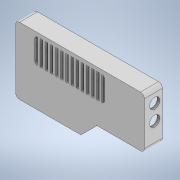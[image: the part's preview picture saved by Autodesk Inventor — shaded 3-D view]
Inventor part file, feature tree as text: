
AUTODESK INVENTOR PART (.ipt)
format: ipt  version: 2021 (Build 250183000, 183)  size: 543,744 bytes
history: native  units: mm
features: sketch x24, extrude x23, chamfer x5, fillet x3, hole x1
ambient origin geometry x8: Origin, YZ Plane, XZ Plane, XY Plane, X Axis, Y Axis, Z Axis, Center Point
bodies: Solid1 (feature_tree)
feature tree (56):
  extrude  "Extrusion1"  Depth=100.0mm
  extrude  "Extrusion3"  Depth=50.0mm
  extrude  "Extrusion4"  Depth=12.5mm
  extrude  "Extrusion12"  Depth=3.0mm TaperAngle=0.0deg
  extrude  "Extrusion13"  Depth=3.0mm TaperAngle=0.0deg
  fillet  "Fillet3"  Radius=2.0mm
  extrude  "Extrusion14"  Depth=2.0mm
  extrude  "Extrusion15"  Depth=44.0mm
  extrude  "Extrusion16"  Depth=12.0mm TaperAngle=0.0deg
  extrude  "Extrusion18"  Depth=12.6mm
  extrude  "Extrusion19"  Depth=3.0mm
  extrude  "Extrusion20"  Depth=1.5mm TaperAngle=0.0deg
  extrude  "Extrusion21"  Depth=4.4mm TaperAngle=0.0deg
  extrude  "Extrusion22"  Depth=2.0mm TaperAngle=0.0deg
  extrude  "Extrusion23"  Depth=14.0mm
  extrude  "Extrusion25"  Depth=4.4mm TaperAngle=0.0deg
  extrude  "Extrusion26"  Depth=4.0mm
  hole  "Hole2"  [1 undecoded]
  chamfer  "Chamfer3"  Distance=12.0mm
  chamfer  "Chamfer4"  Distance=12.0mm
  chamfer  "Chamfer5"  Distance=2.0mm
  chamfer  "Chamfer6"  Distance=12.0mm
  chamfer  "Chamfer7"  Distance=8.0mm
  extrude  "Extrusion27"  Depth=8.0mm
  fillet  "Fillet4"  Radius=8.0mm
  extrude  "Extrusion28"  Depth=2.0mm TaperAngle=0.0deg
  extrude  "Extrusion29"  Depth=1.6mm
  extrude  "Extrusion30"  Depth=0.5mm
  fillet  "Fillet5"  Radius=9.4mm
  extrude  "Extrusion31"  Depth=3.0mm
  extrude  "Extrusion32"  Depth=3.0mm
  extrude  "Extrusion33"  Depth=3.0mm
  sketch  "Sketch1"  dims[d0=52.0mm d1=100.0mm]
  sketch  "Sketch4"  dims[d2=26.0mm d3=50.0mm]
  sketch  "Sketch5"  dims[d4=2.0mm d5=0.0mm d35=12.5mm]
  sketch  "Sketch13"  dims[d36=63.1mm d37=3.0mm d38=0.0mm]
  sketch  "Sketch14"  dims[d39=50.673mm d40=3.0mm d41=0.0mm d79=2.0mm]
  sketch  "Sketch15"  dims[d80=2.0mm d81=2.0mm]
  sketch  "Sketch16"  dims[d82=1.2mm d83=44.0mm]
  sketch  "Sketch17"  dims[d84=59.0mm d85=12.0mm d86=0.0mm]
  sketch  "Sketch19"  dims[d87=2.0mm d88=12.6mm]
  sketch  "Sketch20"  dims[d89=12.0mm d90=0.0mm d91=3.0mm]
  sketch  "Sketch21"  dims[d92=7.8mm d93=1.5mm d94=0.0mm]
  sketch  "Sketch22"  dims[d95=33.8mm d96=4.4mm d97=0.0mm]
  sketch  "Sketch23"  dims[d98=2.0mm d99=2.0mm d100=0.0mm]
  sketch  "Sketch24"  dims[d108=3.0mm d109=14.0mm]
  sketch  "Sketch26"  dims[d110=10.0mm d111=4.4mm d112=0.0mm]
  sketch  "Sketch27"  dims[d113=1.3mm d114=4.0mm]
  sketch  "Sketch28"  dims[d115=3.0mm d116=0.0mm d117=2.0mm]
  sketch  "Sketch29"  dims[d118=2.0mm d119=12.0mm d120=0.0mm d121=12.0mm d122=0.0mm]
  sketch  "Sketch30"  dims[d123=70.0mm]
  sketch  "Sketch31"  dims[d124=89.0mm]
  sketch  "Sketch32"  dims[d125=8.0mm]
  sketch  "Sketch33"  dims[d126=8.0mm d127=2.0mm d128=0.0mm]
  sketch  "Sketch34"  dims[d129=8.0mm]
  sketch  "Sketch35"  dims[d130=10.0mm d131=12.0mm d132=8.0mm d133=8.0mm d134=8.0mm d135=2.0mm d136=0.0mm d140=1.6mm d141=0.5mm d142=9.4mm d143=0.0mm d144=3.0mm d145=3.0mm d146=3.0mm d147=50.0mm d148=97.0mm d149=15.0mm d150=3.0mm d151=3.0mm d152=97.0mm d153=49.0mm d154=4.8mm d155=4.8mm d156=4.8mm d157=4.8mm d158=4.8mm d159=5.0mm d160=0.0mm d161=2.0mm d162=6.0mm d163=4.0mm d164=2.0mm d165=90.0deg d166=4.0mm d167=20.594885mm d168=2.0mm d169=2.0mm d170=45.0deg d171=1.0mm d172=2.0mm d173=45.0deg d174=2.0mm d175=2.0mm d176=45.0deg d177=2.0mm d178=2.0mm d179=45.0deg d180=0.8mm d181=2.0mm d182=45.0deg d184=68.0mm d189=2.0mm d190=0.0mm d191=2.0mm d192=2.0mm d193=24.0mm d194=2.0mm d195=0.0mm d196=36.5mm d197=46.5mm d198=3.5mm d199=2.0mm d200=0.0mm d201=12.5mm d202=23.0mm d203=3.5mm d204=2.0mm d205=0.0mm d206=1.0mm d207=8.0mm d208=1.0mm d209=0.0mm d210=1.2mm d211=1.2mm d212=9.1mm d213=0.0mm d214=0.2mm d215=3.0mm d216=0.0mm d67=0.5mm d68=0.872665mm d69=0.5mm d70=0.872665mm d71=0.5mm d72=0.872665mm d73=0.5mm d74=0.872665mm d75=0.872665mm d76=0.5mm d77=0.872665mm]
note: 1 required parameter value undecoded (feature->parameter linkage not recoverable at this tier; creation-order binding heuristic only, values carry confidence <= 0.55)
